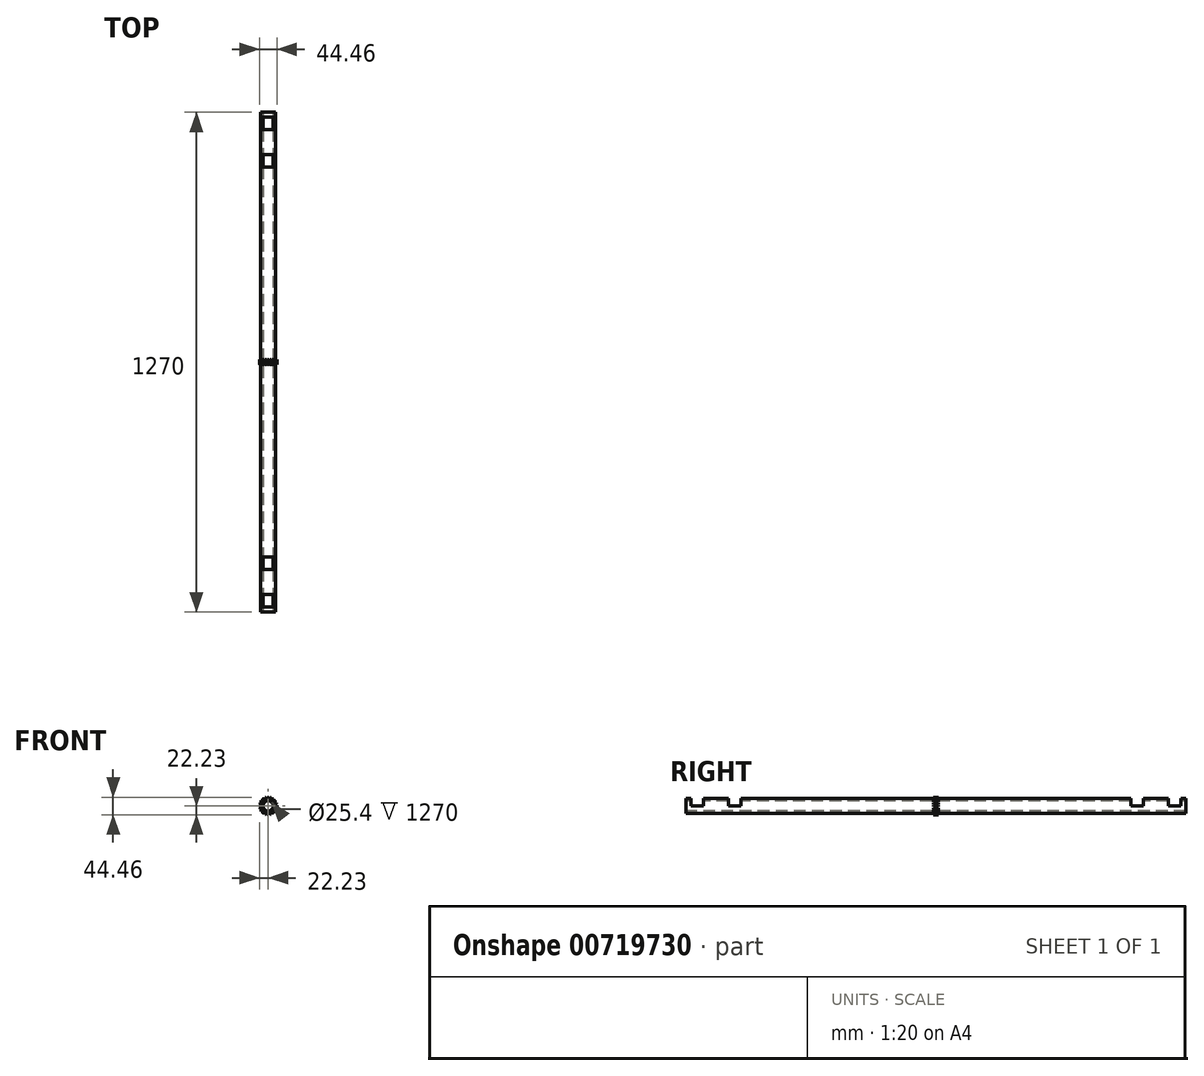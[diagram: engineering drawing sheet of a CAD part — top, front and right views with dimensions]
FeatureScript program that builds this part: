
annotation { "Feature Type Name" : "Feature", "Feature Type Description" : "" }
export const myFeature = defineFeature(function(context is Context, id is Id, definition is map)
    precondition{}
    {
        {
            var Q0;
            Q0=qCreatedBy(makeId("Front.planeOp"),FACE);
            var sketch = newSketch(context, id + "F0", { "sketchPlane" : qUnion([Q0])});
            skCircle(sketch, "E0", {"center": v(0, 0) * mm, "radius": 19.05 * mm});
            skSolve(sketch);
        }
        {
            var Q0;
            Q0 = qSketchRegion(id + "F0", true);
            extrude(context, id + "F1", {"entities" : qUnion([Q0]), "depth" : 1270 * mm, "offsetDistance" : 25.4 * mm});
        }
        {
            var Q0;
            Q0=makeQuery(id+"F1.opExtrude","CAP_FACE",FACE,{"disambiguationData":[OSD([sQuery(id+"F0.wireOp",EDGE,"E0")])],"isStart":false});
            cPlane(context, id + "F2", {"entities" : qUnion([Q0]), "cplaneType" : CPlaneType.OFFSET, "offset" : 635 * mm, "oppositeDirection" : true, "width" : 152.4 * mm, "height" : 152.4 * mm});
        }
        {
            var Q0;
            Q0=qCreatedBy(id+"F2.planeOp",FACE);
            var sketch = newSketch(context, id + "F3", { "sketchPlane" : qUnion([Q0])});
            skCircle(sketch, "E1", {"center": v(0, 0) * mm, "radius": 22.23 * mm});
            skCircle(sketch, "E2", {"center": v(0, 0) * mm, "radius": 19.05 * mm, "construction": true});
            skLineSegment(sketch, "E3.bottom", {"start": v(-1.52, 18.99) * mm, "end": v(1.52, 18.95) * mm});
            skLineSegment(sketch, "E3.left", {"start": v(-1.52, 18.99) * mm, "end": v(-1.52, 19.74) * mm});
            skLineSegment(sketch, "E3.right", {"start": v(1.52, 18.95) * mm, "end": v(1.52, 19.74) * mm});
            skLineSegment(sketch, "E4", {"start": v(0, 0) * mm, "end": v(0, 22.23) * mm, "construction": true});
            skLineSegment(sketch, "E5", {"start": v(-1.17, 21.35) * mm, "end": v(-0.76, 22.21) * mm});
            skPoint(sketch, "E6.orphan", {"position": v(-1.52, 22.17) * mm});
            skLineSegment(sketch, "E7.MirrorCS", {"start": v(1.17, 21.35) * mm, "end": v(0.76, 22.21) * mm});
            skPoint(sketch, "E8.visualSharp", {"position": v(-1.52, 20.58) * mm});
            skArc(sketch, "E8.filletArc", {"start": v(-1.17, 21.35) * mm, "mid": v(-1.43, 20.56) * mm, "end": v(-1.52, 19.74) * mm});
            skArc(sketch, "E9.MirrorCS", {"start": v(1.17, 21.35) * mm, "mid": v(1.43, 20.56) * mm, "end": v(1.52, 19.74) * mm});
            skPoint(sketch, "E10.orphan", {"position": v(1.52, 20.58) * mm});
            skLineSegment(sketch, "E11.1.0", {"start": v(-5.49, 20.66) * mm, "end": v(-6.14, 21.36) * mm});
            skArc(sketch, "E11.1.1", {"start": v(-5.49, 20.66) * mm, "mid": v(-5, 20) * mm, "end": v(-4.65, 19.24) * mm});
            skLineSegment(sketch, "E11.1.2", {"start": v(-4.4, 18.5) * mm, "end": v(-4.65, 19.24) * mm});
            skLineSegment(sketch, "E11.1.3", {"start": v(-7.32, 17.59) * mm, "end": v(-4.4, 18.5) * mm});
            skLineSegment(sketch, "E11.1.4", {"start": v(-7.32, 17.59) * mm, "end": v(-7.55, 18.3) * mm});
            skArc(sketch, "E11.1.5", {"start": v(-7.7, 19.94) * mm, "mid": v(-7.72, 19.11) * mm, "end": v(-7.55, 18.3) * mm});
            skLineSegment(sketch, "E11.1.6", {"start": v(-7.7, 19.94) * mm, "end": v(-7.59, 20.89) * mm});
            skLineSegment(sketch, "E11.2.0", {"start": v(-11.6, 17.96) * mm, "end": v(-12.44, 18.42) * mm});
            skArc(sketch, "E11.2.1", {"start": v(-11.6, 17.96) * mm, "mid": v(-10.93, 17.48) * mm, "end": v(-10.37, 16.86) * mm});
            skLineSegment(sketch, "E11.2.2", {"start": v(-9.9, 16.23) * mm, "end": v(-10.37, 16.86) * mm});
            skLineSegment(sketch, "E11.2.3", {"start": v(-12.4, 14.47) * mm, "end": v(-9.9, 16.23) * mm});
            skLineSegment(sketch, "E11.2.4", {"start": v(-12.4, 14.47) * mm, "end": v(-12.83, 15.07) * mm});
            skArc(sketch, "E11.2.5", {"start": v(-13.5, 16.59) * mm, "mid": v(-13.25, 15.8) * mm, "end": v(-12.83, 15.07) * mm});
            skLineSegment(sketch, "E11.2.6", {"start": v(-13.5, 16.59) * mm, "end": v(-13.67, 17.52) * mm});
            skLineSegment(sketch, "E11.3.0", {"start": v(-16.59, 13.5) * mm, "end": v(-17.52, 13.67) * mm});
            skArc(sketch, "E11.3.1", {"start": v(-16.59, 13.5) * mm, "mid": v(-15.8, 13.25) * mm, "end": v(-15.07, 12.83) * mm});
            skLineSegment(sketch, "E11.3.2", {"start": v(-14.43, 12.37) * mm, "end": v(-15.07, 12.83) * mm});
            skLineSegment(sketch, "E11.3.3", {"start": v(-16.26, 9.93) * mm, "end": v(-14.43, 12.37) * mm});
            skLineSegment(sketch, "E11.3.4", {"start": v(-16.26, 9.93) * mm, "end": v(-16.86, 10.37) * mm});
            skArc(sketch, "E11.3.5", {"start": v(-17.96, 11.6) * mm, "mid": v(-17.48, 10.93) * mm, "end": v(-16.86, 10.37) * mm});
            skLineSegment(sketch, "E11.3.6", {"start": v(-17.96, 11.6) * mm, "end": v(-18.42, 12.44) * mm});
            skLineSegment(sketch, "E11.4.0", {"start": v(-19.94, 7.7) * mm, "end": v(-20.89, 7.59) * mm});
            skArc(sketch, "E11.4.1", {"start": v(-19.94, 7.7) * mm, "mid": v(-19.11, 7.72) * mm, "end": v(-18.3, 7.55) * mm});
            skLineSegment(sketch, "E11.4.2", {"start": v(-17.55, 7.3) * mm, "end": v(-18.3, 7.55) * mm});
            skLineSegment(sketch, "E11.4.3", {"start": v(-18.53, 4.42) * mm, "end": v(-17.55, 7.3) * mm});
            skLineSegment(sketch, "E11.4.4", {"start": v(-18.53, 4.42) * mm, "end": v(-19.24, 4.65) * mm});
            skArc(sketch, "E11.4.5", {"start": v(-20.66, 5.49) * mm, "mid": v(-20, 5) * mm, "end": v(-19.24, 4.65) * mm});
            skLineSegment(sketch, "E11.4.6", {"start": v(-20.66, 5.49) * mm, "end": v(-21.36, 6.14) * mm});
            skLineSegment(sketch, "E11.5.0", {"start": v(-21.35, 1.17) * mm, "end": v(-22.21, 0.76) * mm});
            skArc(sketch, "E11.5.1", {"start": v(-21.35, 1.17) * mm, "mid": v(-20.56, 1.43) * mm, "end": v(-19.74, 1.52) * mm});
            skLineSegment(sketch, "E11.5.2", {"start": v(-18.95, 1.52) * mm, "end": v(-19.74, 1.52) * mm});
            skLineSegment(sketch, "E11.5.3", {"start": v(-18.99, -1.52) * mm, "end": v(-18.95, 1.52) * mm});
            skLineSegment(sketch, "E11.5.4", {"start": v(-18.99, -1.52) * mm, "end": v(-19.74, -1.52) * mm});
            skArc(sketch, "E11.5.5", {"start": v(-21.35, -1.17) * mm, "mid": v(-20.56, -1.43) * mm, "end": v(-19.74, -1.52) * mm});
            skLineSegment(sketch, "E11.5.6", {"start": v(-21.35, -1.17) * mm, "end": v(-22.21, -0.76) * mm});
            skLineSegment(sketch, "E11.6.0", {"start": v(-20.66, -5.49) * mm, "end": v(-21.36, -6.14) * mm});
            skArc(sketch, "E11.6.1", {"start": v(-20.66, -5.49) * mm, "mid": v(-20, -5) * mm, "end": v(-19.24, -4.65) * mm});
            skLineSegment(sketch, "E11.6.2", {"start": v(-18.5, -4.4) * mm, "end": v(-19.24, -4.65) * mm});
            skLineSegment(sketch, "E11.6.3", {"start": v(-17.59, -7.32) * mm, "end": v(-18.5, -4.4) * mm});
            skLineSegment(sketch, "E11.6.4", {"start": v(-17.59, -7.32) * mm, "end": v(-18.3, -7.55) * mm});
            skArc(sketch, "E11.6.5", {"start": v(-19.94, -7.7) * mm, "mid": v(-19.11, -7.72) * mm, "end": v(-18.3, -7.55) * mm});
            skLineSegment(sketch, "E11.6.6", {"start": v(-19.94, -7.7) * mm, "end": v(-20.89, -7.59) * mm});
            skLineSegment(sketch, "E11.7.0", {"start": v(-17.96, -11.6) * mm, "end": v(-18.42, -12.44) * mm});
            skArc(sketch, "E11.7.1", {"start": v(-17.96, -11.6) * mm, "mid": v(-17.48, -10.93) * mm, "end": v(-16.86, -10.37) * mm});
            skLineSegment(sketch, "E11.7.2", {"start": v(-16.23, -9.9) * mm, "end": v(-16.86, -10.37) * mm});
            skLineSegment(sketch, "E11.7.3", {"start": v(-14.47, -12.4) * mm, "end": v(-16.23, -9.9) * mm});
            skLineSegment(sketch, "E11.7.4", {"start": v(-14.47, -12.4) * mm, "end": v(-15.07, -12.83) * mm});
            skArc(sketch, "E11.7.5", {"start": v(-16.59, -13.5) * mm, "mid": v(-15.8, -13.25) * mm, "end": v(-15.07, -12.83) * mm});
            skLineSegment(sketch, "E11.7.6", {"start": v(-16.59, -13.5) * mm, "end": v(-17.52, -13.67) * mm});
            skLineSegment(sketch, "E11.8.0", {"start": v(-13.5, -16.59) * mm, "end": v(-13.67, -17.52) * mm});
            skArc(sketch, "E11.8.1", {"start": v(-13.5, -16.59) * mm, "mid": v(-13.25, -15.8) * mm, "end": v(-12.83, -15.07) * mm});
            skLineSegment(sketch, "E11.8.2", {"start": v(-12.37, -14.43) * mm, "end": v(-12.83, -15.07) * mm});
            skLineSegment(sketch, "E11.8.3", {"start": v(-9.93, -16.26) * mm, "end": v(-12.37, -14.43) * mm});
            skLineSegment(sketch, "E11.8.4", {"start": v(-9.93, -16.26) * mm, "end": v(-10.37, -16.86) * mm});
            skArc(sketch, "E11.8.5", {"start": v(-11.6, -17.96) * mm, "mid": v(-10.93, -17.48) * mm, "end": v(-10.37, -16.86) * mm});
            skLineSegment(sketch, "E11.8.6", {"start": v(-11.6, -17.96) * mm, "end": v(-12.44, -18.42) * mm});
            skLineSegment(sketch, "E11.9.0", {"start": v(-7.7, -19.94) * mm, "end": v(-7.59, -20.89) * mm});
            skArc(sketch, "E11.9.1", {"start": v(-7.7, -19.94) * mm, "mid": v(-7.72, -19.11) * mm, "end": v(-7.55, -18.3) * mm});
            skLineSegment(sketch, "E11.9.2", {"start": v(-7.3, -17.55) * mm, "end": v(-7.55, -18.3) * mm});
            skLineSegment(sketch, "E11.9.3", {"start": v(-4.42, -18.53) * mm, "end": v(-7.3, -17.55) * mm});
            skLineSegment(sketch, "E11.9.4", {"start": v(-4.42, -18.53) * mm, "end": v(-4.65, -19.24) * mm});
            skArc(sketch, "E11.9.5", {"start": v(-5.49, -20.66) * mm, "mid": v(-5, -20) * mm, "end": v(-4.65, -19.24) * mm});
            skLineSegment(sketch, "E11.9.6", {"start": v(-5.49, -20.66) * mm, "end": v(-6.14, -21.36) * mm});
            skLineSegment(sketch, "E11.10.0", {"start": v(-1.17, -21.35) * mm, "end": v(-0.76, -22.21) * mm});
            skArc(sketch, "E11.10.1", {"start": v(-1.17, -21.35) * mm, "mid": v(-1.43, -20.56) * mm, "end": v(-1.52, -19.74) * mm});
            skLineSegment(sketch, "E11.10.2", {"start": v(-1.52, -18.95) * mm, "end": v(-1.52, -19.74) * mm});
            skLineSegment(sketch, "E11.10.3", {"start": v(1.52, -18.99) * mm, "end": v(-1.52, -18.95) * mm});
            skLineSegment(sketch, "E11.10.4", {"start": v(1.52, -18.99) * mm, "end": v(1.52, -19.74) * mm});
            skArc(sketch, "E11.10.5", {"start": v(1.17, -21.35) * mm, "mid": v(1.43, -20.56) * mm, "end": v(1.52, -19.74) * mm});
            skLineSegment(sketch, "E11.10.6", {"start": v(1.17, -21.35) * mm, "end": v(0.76, -22.21) * mm});
            skLineSegment(sketch, "E11.11.0", {"start": v(5.49, -20.66) * mm, "end": v(6.14, -21.36) * mm});
            skArc(sketch, "E11.11.1", {"start": v(5.49, -20.66) * mm, "mid": v(5, -20) * mm, "end": v(4.65, -19.24) * mm});
            skLineSegment(sketch, "E11.11.2", {"start": v(4.4, -18.5) * mm, "end": v(4.65, -19.24) * mm});
            skLineSegment(sketch, "E11.11.3", {"start": v(7.32, -17.59) * mm, "end": v(4.4, -18.5) * mm});
            skLineSegment(sketch, "E11.11.4", {"start": v(7.32, -17.59) * mm, "end": v(7.55, -18.3) * mm});
            skArc(sketch, "E11.11.5", {"start": v(7.7, -19.94) * mm, "mid": v(7.72, -19.11) * mm, "end": v(7.55, -18.3) * mm});
            skLineSegment(sketch, "E11.11.6", {"start": v(7.7, -19.94) * mm, "end": v(7.59, -20.89) * mm});
            skLineSegment(sketch, "E11.12.0", {"start": v(11.6, -17.96) * mm, "end": v(12.44, -18.42) * mm});
            skArc(sketch, "E11.12.1", {"start": v(11.6, -17.96) * mm, "mid": v(10.93, -17.48) * mm, "end": v(10.37, -16.86) * mm});
            skLineSegment(sketch, "E11.12.2", {"start": v(9.9, -16.23) * mm, "end": v(10.37, -16.86) * mm});
            skLineSegment(sketch, "E11.12.3", {"start": v(12.4, -14.47) * mm, "end": v(9.9, -16.23) * mm});
            skLineSegment(sketch, "E11.12.4", {"start": v(12.4, -14.47) * mm, "end": v(12.83, -15.07) * mm});
            skArc(sketch, "E11.12.5", {"start": v(13.5, -16.59) * mm, "mid": v(13.25, -15.8) * mm, "end": v(12.83, -15.07) * mm});
            skLineSegment(sketch, "E11.12.6", {"start": v(13.5, -16.59) * mm, "end": v(13.67, -17.52) * mm});
            skLineSegment(sketch, "E11.13.0", {"start": v(16.59, -13.5) * mm, "end": v(17.52, -13.67) * mm});
            skArc(sketch, "E11.13.1", {"start": v(16.59, -13.5) * mm, "mid": v(15.8, -13.25) * mm, "end": v(15.07, -12.83) * mm});
            skLineSegment(sketch, "E11.13.2", {"start": v(14.43, -12.37) * mm, "end": v(15.07, -12.83) * mm});
            skLineSegment(sketch, "E11.13.3", {"start": v(16.26, -9.93) * mm, "end": v(14.43, -12.37) * mm});
            skLineSegment(sketch, "E11.13.4", {"start": v(16.26, -9.93) * mm, "end": v(16.86, -10.37) * mm});
            skArc(sketch, "E11.13.5", {"start": v(17.96, -11.6) * mm, "mid": v(17.48, -10.93) * mm, "end": v(16.86, -10.37) * mm});
            skLineSegment(sketch, "E11.13.6", {"start": v(17.96, -11.6) * mm, "end": v(18.42, -12.44) * mm});
            skLineSegment(sketch, "E11.14.0", {"start": v(19.94, -7.7) * mm, "end": v(20.89, -7.59) * mm});
            skArc(sketch, "E11.14.1", {"start": v(19.94, -7.7) * mm, "mid": v(19.11, -7.72) * mm, "end": v(18.3, -7.55) * mm});
            skLineSegment(sketch, "E11.14.2", {"start": v(17.55, -7.3) * mm, "end": v(18.3, -7.55) * mm});
            skLineSegment(sketch, "E11.14.3", {"start": v(18.53, -4.42) * mm, "end": v(17.55, -7.3) * mm});
            skLineSegment(sketch, "E11.14.4", {"start": v(18.53, -4.42) * mm, "end": v(19.24, -4.65) * mm});
            skArc(sketch, "E11.14.5", {"start": v(20.66, -5.49) * mm, "mid": v(20, -5) * mm, "end": v(19.24, -4.65) * mm});
            skLineSegment(sketch, "E11.14.6", {"start": v(20.66, -5.49) * mm, "end": v(21.36, -6.14) * mm});
            skLineSegment(sketch, "E11.15.0", {"start": v(21.35, -1.17) * mm, "end": v(22.21, -0.76) * mm});
            skArc(sketch, "E11.15.1", {"start": v(21.35, -1.17) * mm, "mid": v(20.56, -1.43) * mm, "end": v(19.74, -1.52) * mm});
            skLineSegment(sketch, "E11.15.2", {"start": v(18.95, -1.52) * mm, "end": v(19.74, -1.52) * mm});
            skLineSegment(sketch, "E11.15.3", {"start": v(18.99, 1.52) * mm, "end": v(18.95, -1.52) * mm});
            skLineSegment(sketch, "E11.15.4", {"start": v(18.99, 1.52) * mm, "end": v(19.74, 1.52) * mm});
            skArc(sketch, "E11.15.5", {"start": v(21.35, 1.17) * mm, "mid": v(20.56, 1.43) * mm, "end": v(19.74, 1.52) * mm});
            skLineSegment(sketch, "E11.15.6", {"start": v(21.35, 1.17) * mm, "end": v(22.21, 0.76) * mm});
            skLineSegment(sketch, "E11.16.0", {"start": v(20.66, 5.49) * mm, "end": v(21.36, 6.14) * mm});
            skArc(sketch, "E11.16.1", {"start": v(20.66, 5.49) * mm, "mid": v(20, 5) * mm, "end": v(19.24, 4.65) * mm});
            skLineSegment(sketch, "E11.16.2", {"start": v(18.5, 4.4) * mm, "end": v(19.24, 4.65) * mm});
            skLineSegment(sketch, "E11.16.3", {"start": v(17.59, 7.32) * mm, "end": v(18.5, 4.4) * mm});
            skLineSegment(sketch, "E11.16.4", {"start": v(17.59, 7.32) * mm, "end": v(18.3, 7.55) * mm});
            skArc(sketch, "E11.16.5", {"start": v(19.94, 7.7) * mm, "mid": v(19.11, 7.72) * mm, "end": v(18.3, 7.55) * mm});
            skLineSegment(sketch, "E11.16.6", {"start": v(19.94, 7.7) * mm, "end": v(20.89, 7.59) * mm});
            skLineSegment(sketch, "E11.17.0", {"start": v(17.96, 11.6) * mm, "end": v(18.42, 12.44) * mm});
            skArc(sketch, "E11.17.1", {"start": v(17.96, 11.6) * mm, "mid": v(17.48, 10.93) * mm, "end": v(16.86, 10.37) * mm});
            skLineSegment(sketch, "E11.17.2", {"start": v(16.23, 9.9) * mm, "end": v(16.86, 10.37) * mm});
            skLineSegment(sketch, "E11.17.3", {"start": v(14.47, 12.4) * mm, "end": v(16.23, 9.9) * mm});
            skLineSegment(sketch, "E11.17.4", {"start": v(14.47, 12.4) * mm, "end": v(15.07, 12.83) * mm});
            skArc(sketch, "E11.17.5", {"start": v(16.59, 13.5) * mm, "mid": v(15.8, 13.25) * mm, "end": v(15.07, 12.83) * mm});
            skLineSegment(sketch, "E11.17.6", {"start": v(16.59, 13.5) * mm, "end": v(17.52, 13.67) * mm});
            skLineSegment(sketch, "E11.18.0", {"start": v(13.5, 16.59) * mm, "end": v(13.67, 17.52) * mm});
            skArc(sketch, "E11.18.1", {"start": v(13.5, 16.59) * mm, "mid": v(13.25, 15.8) * mm, "end": v(12.83, 15.07) * mm});
            skLineSegment(sketch, "E11.18.2", {"start": v(12.37, 14.43) * mm, "end": v(12.83, 15.07) * mm});
            skLineSegment(sketch, "E11.18.3", {"start": v(9.93, 16.26) * mm, "end": v(12.37, 14.43) * mm});
            skLineSegment(sketch, "E11.18.4", {"start": v(9.93, 16.26) * mm, "end": v(10.37, 16.86) * mm});
            skArc(sketch, "E11.18.5", {"start": v(11.6, 17.96) * mm, "mid": v(10.93, 17.48) * mm, "end": v(10.37, 16.86) * mm});
            skLineSegment(sketch, "E11.18.6", {"start": v(11.6, 17.96) * mm, "end": v(12.44, 18.42) * mm});
            skLineSegment(sketch, "E11.19.0", {"start": v(7.7, 19.94) * mm, "end": v(7.59, 20.89) * mm});
            skArc(sketch, "E11.19.1", {"start": v(7.7, 19.94) * mm, "mid": v(7.72, 19.11) * mm, "end": v(7.55, 18.3) * mm});
            skLineSegment(sketch, "E11.19.2", {"start": v(7.3, 17.55) * mm, "end": v(7.55, 18.3) * mm});
            skLineSegment(sketch, "E11.19.3", {"start": v(4.42, 18.53) * mm, "end": v(7.3, 17.55) * mm});
            skLineSegment(sketch, "E11.19.4", {"start": v(4.42, 18.53) * mm, "end": v(4.65, 19.24) * mm});
            skArc(sketch, "E11.19.5", {"start": v(5.49, 20.66) * mm, "mid": v(5, 20) * mm, "end": v(4.65, 19.24) * mm});
            skLineSegment(sketch, "E11.19.6", {"start": v(5.49, 20.66) * mm, "end": v(6.14, 21.36) * mm});
            skSolve(sketch);
        }
        {
            var Q0;
            {var subQ0=sQuery(id+"F3.wireOp",EDGE,"E11.17.0");Q0=makeQuery(id+"F3.imprint","IMPRINT",FACE,{"disambiguationData":[TD([[makeQuery(id+"F3.imprint","IMPRINT",EDGE,{"derivedFrom":subQ0}),1.0]])]});}
            var Q1;
            {var subQ0=sQuery(id+"F3.wireOp",EDGE,"E11.18.0");Q1=makeQuery(id+"F3.imprint","IMPRINT",FACE,{"disambiguationData":[TD([[makeQuery(id+"F3.imprint","IMPRINT",EDGE,{"derivedFrom":subQ0}),1.0]])]});}
            var Q2;
            {var subQ0=sQuery(id+"F3.wireOp",EDGE,"E11.19.0");Q2=makeQuery(id+"F3.imprint","IMPRINT",FACE,{"disambiguationData":[TD([[makeQuery(id+"F3.imprint","IMPRINT",EDGE,{"derivedFrom":subQ0}),1.0]])]});}
            var Q3;
            Q3=makeQuery(id+"F3.imprint","IMPRINT",FACE,{"disambiguationData":[TD([[makeQuery(id+"F3.imprint","IMPRINT",EDGE,{"derivedFrom":sQuery(id+"F3.wireOp",EDGE,"E3.bottom")}),1.0]])]});
            var Q4;
            {var subQ0=sQuery(id+"F3.wireOp",EDGE,"E11.1.0");Q4=makeQuery(id+"F3.imprint","IMPRINT",FACE,{"disambiguationData":[TD([[makeQuery(id+"F3.imprint","IMPRINT",EDGE,{"derivedFrom":subQ0}),1.0]])]});}
            var Q5;
            {var subQ0=sQuery(id+"F3.wireOp",EDGE,"E11.2.0");Q5=makeQuery(id+"F3.imprint","IMPRINT",FACE,{"disambiguationData":[TD([[makeQuery(id+"F3.imprint","IMPRINT",EDGE,{"derivedFrom":subQ0}),1.0]])]});}
            var Q6;
            {var subQ0=sQuery(id+"F3.wireOp",EDGE,"E11.3.0");Q6=makeQuery(id+"F3.imprint","IMPRINT",FACE,{"disambiguationData":[TD([[makeQuery(id+"F3.imprint","IMPRINT",EDGE,{"derivedFrom":subQ0}),1.0]])]});}
            var Q7;
            {var subQ0=sQuery(id+"F3.wireOp",EDGE,"E11.4.0");Q7=makeQuery(id+"F3.imprint","IMPRINT",FACE,{"disambiguationData":[TD([[makeQuery(id+"F3.imprint","IMPRINT",EDGE,{"derivedFrom":subQ0}),1.0]])]});}
            var Q8;
            {var subQ0=sQuery(id+"F3.wireOp",EDGE,"E11.5.0");Q8=makeQuery(id+"F3.imprint","IMPRINT",FACE,{"disambiguationData":[TD([[makeQuery(id+"F3.imprint","IMPRINT",EDGE,{"derivedFrom":subQ0}),1.0]])]});}
            var Q9;
            {var subQ0=sQuery(id+"F3.wireOp",EDGE,"E11.6.0");Q9=makeQuery(id+"F3.imprint","IMPRINT",FACE,{"disambiguationData":[TD([[makeQuery(id+"F3.imprint","IMPRINT",EDGE,{"derivedFrom":subQ0}),1.0]])]});}
            var Q10;
            {var subQ0=sQuery(id+"F3.wireOp",EDGE,"E11.7.0");Q10=makeQuery(id+"F3.imprint","IMPRINT",FACE,{"disambiguationData":[TD([[makeQuery(id+"F3.imprint","IMPRINT",EDGE,{"derivedFrom":subQ0}),1.0]])]});}
            var Q11;
            {var subQ0=sQuery(id+"F3.wireOp",EDGE,"E11.8.0");Q11=makeQuery(id+"F3.imprint","IMPRINT",FACE,{"disambiguationData":[TD([[makeQuery(id+"F3.imprint","IMPRINT",EDGE,{"derivedFrom":subQ0}),1.0]])]});}
            var Q12;
            {var subQ0=sQuery(id+"F3.wireOp",EDGE,"E11.9.0");Q12=makeQuery(id+"F3.imprint","IMPRINT",FACE,{"disambiguationData":[TD([[makeQuery(id+"F3.imprint","IMPRINT",EDGE,{"derivedFrom":subQ0}),1.0]])]});}
            var Q13;
            {var subQ0=sQuery(id+"F3.wireOp",EDGE,"E11.10.0");Q13=makeQuery(id+"F3.imprint","IMPRINT",FACE,{"disambiguationData":[TD([[makeQuery(id+"F3.imprint","IMPRINT",EDGE,{"derivedFrom":subQ0}),1.0]])]});}
            var Q14;
            {var subQ0=sQuery(id+"F3.wireOp",EDGE,"E11.11.0");Q14=makeQuery(id+"F3.imprint","IMPRINT",FACE,{"disambiguationData":[TD([[makeQuery(id+"F3.imprint","IMPRINT",EDGE,{"derivedFrom":subQ0}),1.0]])]});}
            var Q15;
            {var subQ0=sQuery(id+"F3.wireOp",EDGE,"E11.12.0");Q15=makeQuery(id+"F3.imprint","IMPRINT",FACE,{"disambiguationData":[TD([[makeQuery(id+"F3.imprint","IMPRINT",EDGE,{"derivedFrom":subQ0}),1.0]])]});}
            var Q16;
            {var subQ0=sQuery(id+"F3.wireOp",EDGE,"E11.13.0");Q16=makeQuery(id+"F3.imprint","IMPRINT",FACE,{"disambiguationData":[TD([[makeQuery(id+"F3.imprint","IMPRINT",EDGE,{"derivedFrom":subQ0}),1.0]])]});}
            var Q17;
            {var subQ0=sQuery(id+"F3.wireOp",EDGE,"E11.14.0");Q17=makeQuery(id+"F3.imprint","IMPRINT",FACE,{"disambiguationData":[TD([[makeQuery(id+"F3.imprint","IMPRINT",EDGE,{"derivedFrom":subQ0}),1.0]])]});}
            var Q18;
            {var subQ0=sQuery(id+"F3.wireOp",EDGE,"E11.15.0");Q18=makeQuery(id+"F3.imprint","IMPRINT",FACE,{"disambiguationData":[TD([[makeQuery(id+"F3.imprint","IMPRINT",EDGE,{"derivedFrom":subQ0}),1.0]])]});}
            var Q19;
            {var subQ0=sQuery(id+"F3.wireOp",EDGE,"E11.16.0");Q19=makeQuery(id+"F3.imprint","IMPRINT",FACE,{"disambiguationData":[TD([[makeQuery(id+"F3.imprint","IMPRINT",EDGE,{"derivedFrom":subQ0}),1.0]])]});}
            extrude(context, id + "F4", {"entities" : qUnion([Q0, Q1, Q2, Q3, Q4, Q5, Q6, Q7, Q8, Q9, Q10, Q11, Q12, Q13, Q14, Q15, Q16, Q17, Q18, Q19]), "operationType" : NewBodyOperationType.ADD, "endBound" : BoundingType.SYMMETRIC, "depth" : 12.7 * mm, "offsetDistance" : 25.4 * mm});
        }
        {
            var Q0;
            Q0=makeQuery(id+"F1.opExtrude","CAP_FACE",FACE,{"disambiguationData":[OSD([sQuery(id+"F0.wireOp",EDGE,"E0")])],"isStart":false});
            var sketch = newSketch(context, id + "F5", { "sketchPlane" : qUnion([Q0])});
            skCircle(sketch, "E12", {"center": v(0, 0) * mm, "radius": 12.7 * mm});
            skSolve(sketch);
        }
        {
            var Q0;
            Q0=makeQuery(id+"F5.imprint","IMPRINT",FACE,{"disambiguationData":[TD([[makeQuery(id+"F5.imprint","IMPRINT",EDGE,{"derivedFrom":sQuery(id+"F5.wireOp",EDGE,"E12")}),1.0]])]});
            extrude(context, id + "F6", {"entities" : qUnion([Q0]), "operationType" : NewBodyOperationType.REMOVE, "oppositeDirection" : true, "depth" : 1270 * mm, "offsetDistance" : 25.4 * mm});
        }
        {
            var Q0;
            Q0=qCreatedBy(makeId("Top.planeOp"),FACE);
            var sketch = newSketch(context, id + "F7", { "sketchPlane" : qUnion([Q0])});
            skLineSegment(sketch, "E13", {"start": v(-19.05, 0) * mm, "end": v(-19.05, -1270) * mm, "construction": true});
            skLineSegment(sketch, "E14", {"start": v(19.05, 0) * mm, "end": v(19.05, -1270) * mm, "construction": true});
            skLineSegment(sketch, "E15.bottom", {"start": v(-19.05, -12.7) * mm, "end": v(19.05, -12.7) * mm});
            skLineSegment(sketch, "E15.top", {"start": v(-19.05, -44.45) * mm, "end": v(19.05, -44.45) * mm});
            skLineSegment(sketch, "E15.left", {"start": v(-19.05, -12.7) * mm, "end": v(-19.05, -44.45) * mm});
            skLineSegment(sketch, "E15.right", {"start": v(19.05, -12.7) * mm, "end": v(19.05, -44.45) * mm});
            skLineSegment(sketch, "E16.MirrorCS", {"start": v(-19.05, -1257.3) * mm, "end": v(19.05, -1257.3) * mm});
            skLineSegment(sketch, "E17.MirrorCS", {"start": v(-19.05, -1225.55) * mm, "end": v(19.05, -1225.55) * mm});
            skLineSegment(sketch, "E18", {"start": v(-19.05, -1225.55) * mm, "end": v(-19.05, -1257.3) * mm});
            skLineSegment(sketch, "E19", {"start": v(19.05, -1257.3) * mm, "end": v(19.05, -1225.55) * mm});
            skLineSegment(sketch, "E20.bottom", {"start": v(-19.05, -107.95) * mm, "end": v(19.05, -107.95) * mm});
            skLineSegment(sketch, "E20.top", {"start": v(-19.05, -139.7) * mm, "end": v(19.05, -139.7) * mm});
            skLineSegment(sketch, "E20.left", {"start": v(-19.05, -107.95) * mm, "end": v(-19.05, -139.7) * mm});
            skLineSegment(sketch, "E20.right", {"start": v(19.05, -107.95) * mm, "end": v(19.05, -139.7) * mm});
            skLineSegment(sketch, "E21.MirrorCS", {"start": v(-19.05, -1162.05) * mm, "end": v(19.05, -1162.05) * mm});
            skLineSegment(sketch, "E22.MirrorCS", {"start": v(-19.05, -1130.3) * mm, "end": v(19.05, -1130.3) * mm});
            skLineSegment(sketch, "E23", {"start": v(-19.05, -1130.3) * mm, "end": v(-19.05, -1162.05) * mm});
            skLineSegment(sketch, "E24", {"start": v(19.05, -1130.3) * mm, "end": v(19.05, -1162.05) * mm});
            skSolve(sketch);
        }
        {
            var Q0;
            Q0 = qSketchRegion(id + "F7", true);
            extrude(context, id + "F8", {"entities" : qUnion([Q0]), "operationType" : NewBodyOperationType.REMOVE, "depth" : 19.05 * mm, "offsetDistance" : 25.4 * mm});
        }
    });
